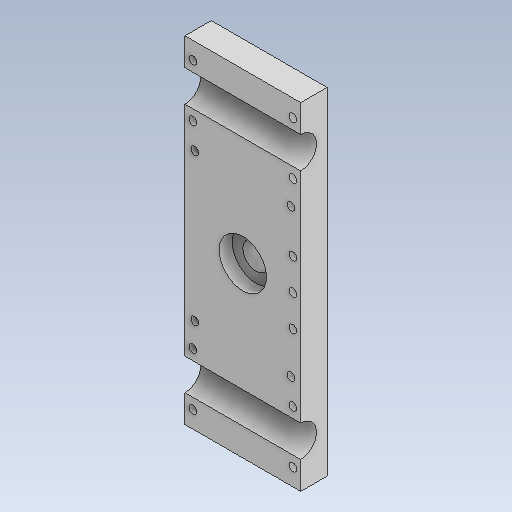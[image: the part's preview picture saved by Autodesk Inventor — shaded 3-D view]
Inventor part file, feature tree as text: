
AUTODESK INVENTOR PART (.ipt)
format: ipt  version: 2020 (Build 240168000, 168)  size: 756,224 bytes
history: native  units: in
note: dims shown in document units (in); Inventor stores cm internally (conversion verified against a paired STEP export)
features: sketch x7, reference x7, other x7, extrude x6
ambient origin geometry x8: Origin, YZ Plane, XZ Plane, XY Plane, X Axis, Y Axis, Z Axis, Center Point
bodies: Solid1 (feature_tree)
feature tree (27):
  extrude  "Extrusion1"  Depth=0.625in
  extrude  "Extrusion2"  Depth=3.0in TaperAngle=0.0deg
  extrude  "Extrusion3"  Depth=3.0in TaperAngle=0.0deg
  extrude  "Extrusion4"  Depth=1.125in
  extrude  "Extrusion5"  Depth=0.625in
  extrude  "Extrusion6"  Depth=0.3125in
  sketch  "Sketch7"  dims[d24=0.25in d25=0.75in d26=0.0in]
  sketch  "Sketch1"  dims[d0=0.625in d1=0.0in d2=0.75in]
  reference  "Reference1"
  reference  "Reference2"
  reference  "Reference3"
  reference  "Reference4"
  sketch  "Sketch2"  dims[d3=0.75in d4=3.0in d5=0.0in]
  sketch  "Sketch3"  dims[d6=0.7874in d8=0.75in d9=0.7874in d11=0.75in d14=3.0in d15=0.0in]
  sketch  "Sketch4"  dims[d16=1.375in d17=1.125in]
  sketch  "Sketch5"  dims[d18=0.3125in d19=0.0in d20=0.625in]
  sketch  "Sketch6"  dims[d21=0.3125in d22=0.0in d23=0.1875in]
  reference  "Reference5"
  reference  "Reference6"
  reference  "Reference7"
  other  "<userpath>\Desktop\PnP Machine\PnP Machine.iam"
  other  "PnP Machine.iam"
  other  "9804K500_LINEAR BRNG HOUSING:3"
  other  "9804K500_LINEAR BRNG HOUSING:4"
  other  "YClampTop:1"
  other  "YClampTop:2"
  other  "6497K113_HIGH-STRENGTH HTD TIMING BELT PULLEY:10"
